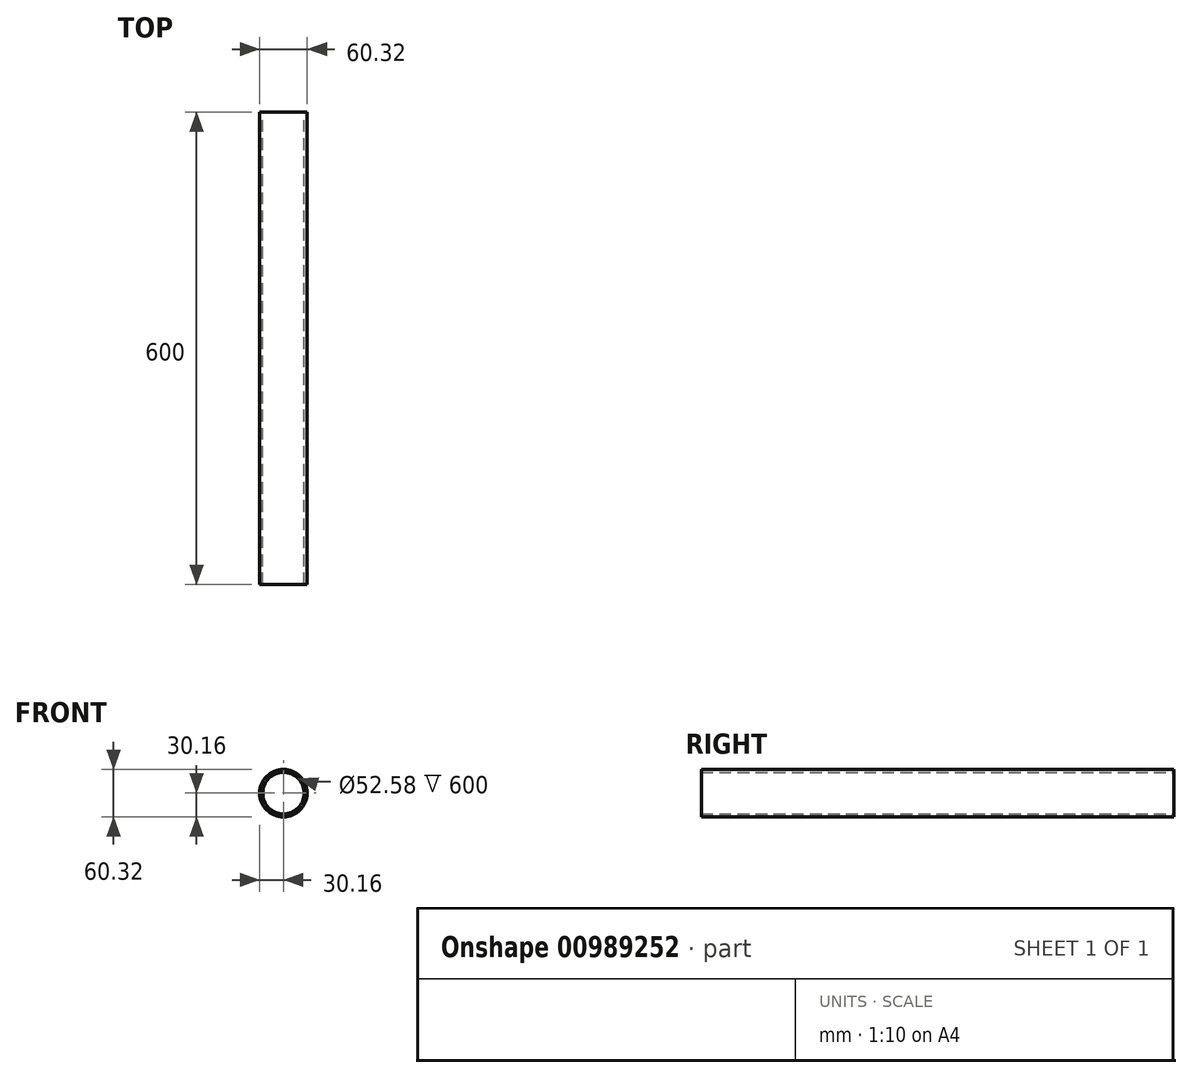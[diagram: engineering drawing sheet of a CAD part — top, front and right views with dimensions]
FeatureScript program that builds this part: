
annotation { "Feature Type Name" : "Feature", "Feature Type Description" : "" }
export const myFeature = defineFeature(function(context is Context, id is Id, definition is map)
    precondition{}
    {
        {
            var Q0;
            Q0=qCreatedBy(makeId("Front.planeOp"),FACE);
            var sketch = newSketch(context, id + "F0", { "sketchPlane" : qUnion([Q0])});
            skCircle(sketch, "E0", {"center": v(0, 0) * mm, "radius": 30.16 * mm});
            skCircle(sketch, "E1", {"center": v(0, 0) * mm, "radius": 26.29 * mm});
            skSolve(sketch);
        }
        {
            var Q0;
            Q0 = qSketchRegion(id + "F0", true);
            extrude(context, id + "F1", {"entities" : qUnion([Q0]), "depth" : 600 * mm, "offsetDistance" : 25 * mm});
        }
    });
